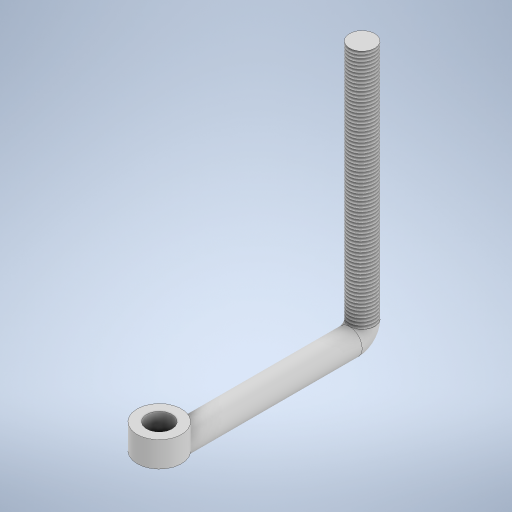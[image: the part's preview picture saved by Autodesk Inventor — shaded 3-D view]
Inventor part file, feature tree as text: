
AUTODESK INVENTOR PART (.ipt)
format: ipt  version: 2024 (Build 280153000, 153)  size: 305,152 bytes
history: native  units: in
note: dims shown in document units (in); Inventor stores cm internally (conversion verified against a paired STEP export)
features: sketch x5, extrude x3, sweep x1, thread x1
ambient origin geometry x8: Origin, YZ Plane, XZ Plane, XY Plane, X Axis, Y Axis, Z Axis, Center Point
bodies: Solid1 (feature_tree)
feature tree (10):
  sweep  "Sweep1"
  thread  "Thread1"  [1 undecoded]
  extrude  "Extrusion1"  TaperAngle=0.0deg  [1 undecoded]
  extrude  "Extrusion2"  Depth=1.378in
  extrude  "Extrusion3"  Depth=0.7874in
  sketch  "Sketch1"  dims[d0=0.7874in d1=6.2992in d2=7.874in]
  sketch  "Sketch2"  dims[d3=0.3937in d4=0.0in d5=0.0in]
  sketch  "Sketch3"  dims[d6=2.7559in d7=0.0in d8=1.378in]
  sketch  "Sketch4"  dims[d9=0.7874in d10=0.0in d11=0.7874in]
  sketch  "Sketch5"  dims[d12=0.0in d13=0.0in d14=0.3937in d15=0.0in]
note: 2 required parameter values undecoded (feature->parameter linkage not recoverable at this tier; creation-order binding heuristic only, values carry confidence <= 0.55)
